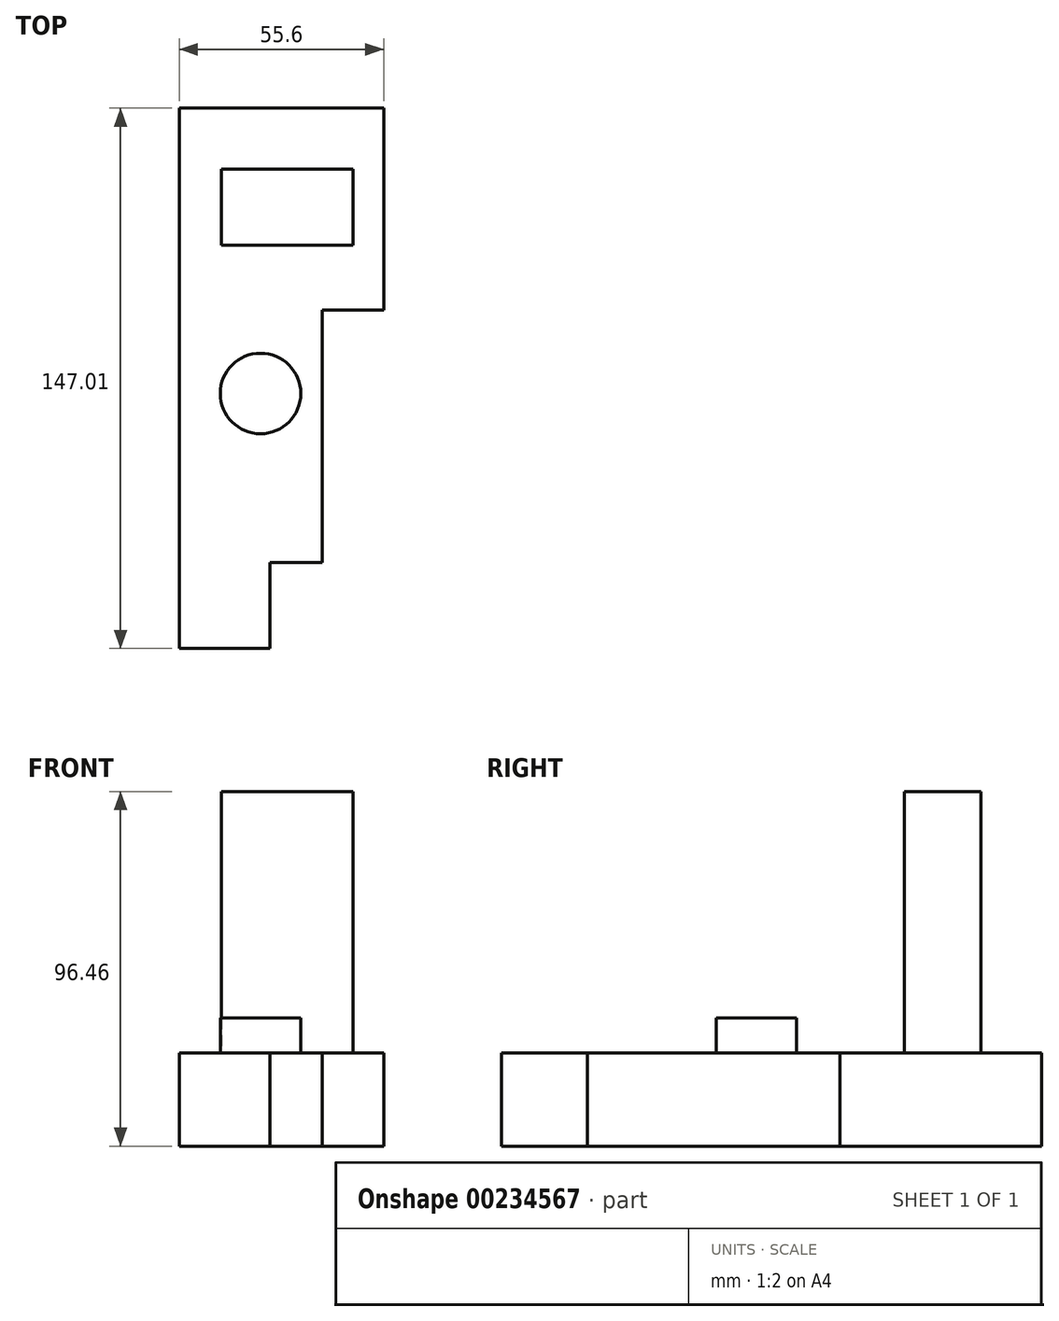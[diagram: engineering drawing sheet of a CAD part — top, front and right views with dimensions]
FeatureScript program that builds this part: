
annotation { "Feature Type Name" : "Feature", "Feature Type Description" : "" }
export const myFeature = defineFeature(function(context is Context, id is Id, definition is map)
    precondition{}
    {
        {
            var Q0;
            Q0=qCreatedBy(makeId("Top.planeOp"),FACE);
            var sketch = newSketch(context, id + "F0", { "sketchPlane" : qUnion([Q0])});
            skLineSegment(sketch, "E0.bottom", {"start": v(-33.32, 0) * mm, "end": v(-35.78, 0) * mm});
            skLineSegment(sketch, "E0.top", {"start": v(-33.32, 0) * mm, "end": v(-35.78, 0) * mm});
            skLineSegment(sketch, "E0.left", {"start": v(-33.32, 0) * mm, "end": v(-33.32, 0) * mm});
            skLineSegment(sketch, "E0.right", {"start": v(-35.78, 0) * mm, "end": v(-35.78, 0) * mm});
            skLineSegment(sketch, "E1.bottom", {"start": v(19.82, 45.11) * mm, "end": v(-35.78, 45.11) * mm});
            skLineSegment(sketch, "E1.top", {"start": v(19.82, 100) * mm, "end": v(-35.78, 100) * mm});
            skLineSegment(sketch, "E1.left", {"start": v(19.82, 45.11) * mm, "end": v(19.82, 100) * mm});
            skLineSegment(sketch, "E1.right", {"start": v(-35.78, 45.11) * mm, "end": v(-35.78, 100) * mm});
            skLineSegment(sketch, "E2.bottom", {"start": v(-35.78, 45.11) * mm, "end": v(-35.78, 45.11) * mm});
            skLineSegment(sketch, "E2.top", {"start": v(-35.78, 154.25) * mm, "end": v(-35.78, 154.25) * mm});
            skLineSegment(sketch, "E2.left", {"start": v(-35.78, 45.11) * mm, "end": v(-35.78, 154.25) * mm});
            skLineSegment(sketch, "E2.right", {"start": v(-35.78, 45.11) * mm, "end": v(-35.78, 154.25) * mm});
            skLineSegment(sketch, "E3.bottom", {"start": v(3.07, -23.65) * mm, "end": v(-27.97, -23.65) * mm});
            skLineSegment(sketch, "E3.top", {"start": v(3.07, 45.11) * mm, "end": v(-27.97, 45.11) * mm});
            skLineSegment(sketch, "E3.left", {"start": v(3.07, -23.65) * mm, "end": v(3.07, 45.11) * mm});
            skLineSegment(sketch, "E3.right", {"start": v(-27.97, -23.65) * mm, "end": v(-27.97, 45.11) * mm});
            skLineSegment(sketch, "E4.bottom", {"start": v(-35.78, 72.55) * mm, "end": v(-11.14, 72.55) * mm});
            skLineSegment(sketch, "E4.top", {"start": v(-35.78, -47.02) * mm, "end": v(-11.14, -47.02) * mm});
            skLineSegment(sketch, "E4.left", {"start": v(-35.78, 72.55) * mm, "end": v(-35.78, -47.02) * mm});
            skLineSegment(sketch, "E4.right", {"start": v(-11.14, 72.55) * mm, "end": v(-11.14, -47.02) * mm});
            skLineSegment(sketch, "E5.bottom", {"start": v(-35.78, -23.9) * mm, "end": v(-11.14, -23.9) * mm, "construction": true});
            skLineSegment(sketch, "E5.top", {"start": v(-35.78, 0) * mm, "end": v(-11.14, 0) * mm, "construction": true});
            skLineSegment(sketch, "E5.left", {"start": v(-35.78, -23.9) * mm, "end": v(-35.78, 0) * mm, "construction": true});
            skLineSegment(sketch, "E5.right", {"start": v(-11.14, -23.9) * mm, "end": v(-11.14, 0) * mm, "construction": true});
            skSolve(sketch);
        }
        {
            var Q0;
            Q0 = qSketchRegion(id + "F0", true);
            extrude(context, id + "F1", {"entities" : qUnion([Q0]), "depth" : 25.4 * mm});
        }
        {
            var Q0;
            Q0=makeQuery(id+"F1.opExtrude","CAP_FACE",FACE,{"disambiguationData":[OSD([sQuery(id+"F0.wireOp",EDGE,"E1.bottom"),sQuery(id+"F0.wireOp",EDGE,"E1.top"),sQuery(id+"F0.wireOp",EDGE,"E1.left"),sQuery(id+"F0.wireOp",EDGE,"E2.right"),sQuery(id+"F0.wireOp",EDGE,"E3.bottom"),sQuery(id+"F0.wireOp",EDGE,"E3.left"),sQuery(id+"F0.wireOp",EDGE,"E4.top"),sQuery(id+"F0.wireOp",EDGE,"E4.left"),sQuery(id+"F0.wireOp",EDGE,"E4.right")])],"isStart":false});
            var sketch = newSketch(context, id + "F2", { "sketchPlane" : qUnion([Q0])});
            skCircle(sketch, "E6", {"center": v(-13.69, 22.34) * mm, "radius": 10.95 * mm});
            skSolve(sketch);
        }
        {
            var Q0;
            Q0 = qSketchRegion(id + "F2", true);
            extrude(context, id + "F3", {"entities" : qUnion([Q0]), "operationType" : NewBodyOperationType.ADD, "depth" : 9.42 * mm});
        }
        {
            var Q0;
            Q0=makeQuery(id+"F1.opExtrude","CAP_FACE",FACE,{"disambiguationData":[OSD([sQuery(id+"F0.wireOp",EDGE,"E1.bottom"),sQuery(id+"F0.wireOp",EDGE,"E1.top"),sQuery(id+"F0.wireOp",EDGE,"E1.left"),sQuery(id+"F0.wireOp",EDGE,"E2.right"),sQuery(id+"F0.wireOp",EDGE,"E3.bottom"),sQuery(id+"F0.wireOp",EDGE,"E3.left"),sQuery(id+"F0.wireOp",EDGE,"E4.top"),sQuery(id+"F0.wireOp",EDGE,"E4.left"),sQuery(id+"F0.wireOp",EDGE,"E4.right")])],"isStart":false});
            var sketch = newSketch(context, id + "F5", { "sketchPlane" : qUnion([Q0])});
            skPoint(sketch, "E7.oppositeSnap0", {"position": v(11.45, 45.11) * mm});
            skLineSegment(sketch, "E7.bottom", {"start": v(-24.35, 83.42) * mm, "end": v(11.45, 83.42) * mm});
            skLineSegment(sketch, "E7.top", {"start": v(-24.35, 62.66) * mm, "end": v(11.45, 62.66) * mm});
            skLineSegment(sketch, "E7.left", {"start": v(-24.35, 83.42) * mm, "end": v(-24.35, 62.66) * mm});
            skLineSegment(sketch, "E7.right", {"start": v(11.45, 83.42) * mm, "end": v(11.45, 62.66) * mm});
            skSolve(sketch);
        }
        {
            var Q0;
            Q0 = qSketchRegion(id + "F5", true);
            extrude(context, id + "F6", {"entities" : qUnion([Q0]), "operationType" : NewBodyOperationType.ADD, "depth" : 71.06 * mm});
        }
    });
